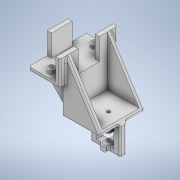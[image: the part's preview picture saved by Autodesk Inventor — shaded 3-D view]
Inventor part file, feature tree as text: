
AUTODESK INVENTOR PART (.ipt)
format: ipt  version: 2020 (Build 240168000, 168)  size: 797,696 bytes
history: native  units: in
note: dims shown in document units (in); Inventor stores cm internally (conversion verified against a paired STEP export)
features: extrude x16, sketch x16, chamfer x3, fillet x3
ambient origin geometry x8: Origin, YZ Plane, XZ Plane, XY Plane, X Axis, Y Axis, Z Axis, Center Point
bodies: Solid1 (feature_tree)
feature tree (38):
  extrude  "Extrusion1"  Depth=2.6378in
  extrude  "Extrusion2"  Depth=0.1969in
  extrude  "Extrusion6"  Depth=0.1969in
  extrude  "Extrusion8"  Depth=1.0in TaperAngle=0.0deg
  chamfer  "Chamfer1"  Distance=1.0in
  extrude  "Extrusion9"  Depth=0.3406in
  extrude  "Extrusion10"  Depth=0.1969in TaperAngle=0.0deg
  extrude  "Extrusion11"  Depth=0.1575in
  extrude  "Extrusion12"  Depth=0.1575in
  extrude  "Extrusion16"  Depth=0.2362in
  extrude  "Extrusion17"  Depth=0.2362in
  extrude  "Extrusion18"  Depth=0.1969in
  extrude  "Extrusion19"  Depth=0.1969in
  extrude  "Extrusion20"  Depth=1.2992in TaperAngle=0.0deg
  chamfer  "Chamfer2"  Distance=0.1969in
  extrude  "Extrusion21"  Depth=0.0787in
  fillet  "Fillet9"  Radius=1.811in
  fillet  "Fillet10"  Radius=0.9055in
  fillet  "Fillet11"  Radius=0.1575in
  extrude  "Extrusion22"  Depth=0.3937in TaperAngle=0.0deg
  extrude  "Extrusion23"  Depth=0.3937in
  chamfer  "Chamfer3"  Distance=0.1575in
  sketch  "Sketch1"  dims[d0=1.4331in d1=2.6378in]
  sketch  "Sketch2"  dims[d2=0.1969in d3=0.0in d4=0.1969in]
  sketch  "Sketch6"  dims[d5=0.8268in d6=0.1969in]
  sketch  "Sketch8"  dims[d7=0.8268in d8=1.0in d9=0.0in]
  sketch  "Sketch9"  dims[d26=0.1969in]
  sketch  "Sketch10"  dims[d27=0.9449in d28=1.0in d29=0.0in]
  sketch  "Sketch11"  dims[d37=0.3406in d38=0.3406in]
  sketch  "Sketch12"  dims[d39=0.3406in d40=0.1969in d41=0.0in]
  sketch  "Sketch16"  dims[d42=0.0591in d43=0.0787in d44=45.0deg d45=0.1575in]
  sketch  "Sketch17"  dims[d46=0.1575in d47=0.1575in]
  sketch  "Sketch18"  dims[d48=0.7874in d49=0.0in d50=0.2362in]
  sketch  "Sketch19"  dims[d51=0.2362in d52=0.2362in]
  sketch  "Sketch20"  dims[d53=0.0984in d54=0.0in d55=0.1969in]
  sketch  "Sketch21"  dims[d56=2.0866in d57=0.1969in]
  sketch  "Sketch22"  dims[d58=0.1969in d59=1.2992in d60=0.0in]
  sketch  "Sketch23"  dims[d61=0.1969in d62=0.1969in d63=0.1969in d64=1.811in d65=0.0in d83=0.9055in d84=0.1575in d85=0.3937in d86=0.0in d87=0.3937in d88=0.1575in d89=0.2953in d90=0.2953in d91=0.2953in d92=0.2953in d93=0.2953in d94=0.2953in d95=0.2953in d96=0.2953in d97=0.6299in d98=0.0in d99=0.6102in d100=0.0in d101=0.2953in d102=0.2953in d103=0.2953in d104=0.2953in d105=0.2953in d106=0.0in d107=0.3543in d108=0.6693in d109=0.0in d110=0.0787in d111=0.0787in d112=45.0deg d113=3.937in d114=0.0in d115=0.0787in d116=0.0787in d117=0.0787in d118=0.5512in d119=1.2402in d120=0.0in d121=0.3937in d122=0.7874in d123=0.0787in d124=0.0in d125=0.0787in d126=0.0787in d127=45.0deg d10=0.0197in d11=0.0344in d13=0.0197in d14=0.0344in d15=0.0197in d16=0.0344in d80=0.0197in d81=0.0344in d82=0.0197in]
